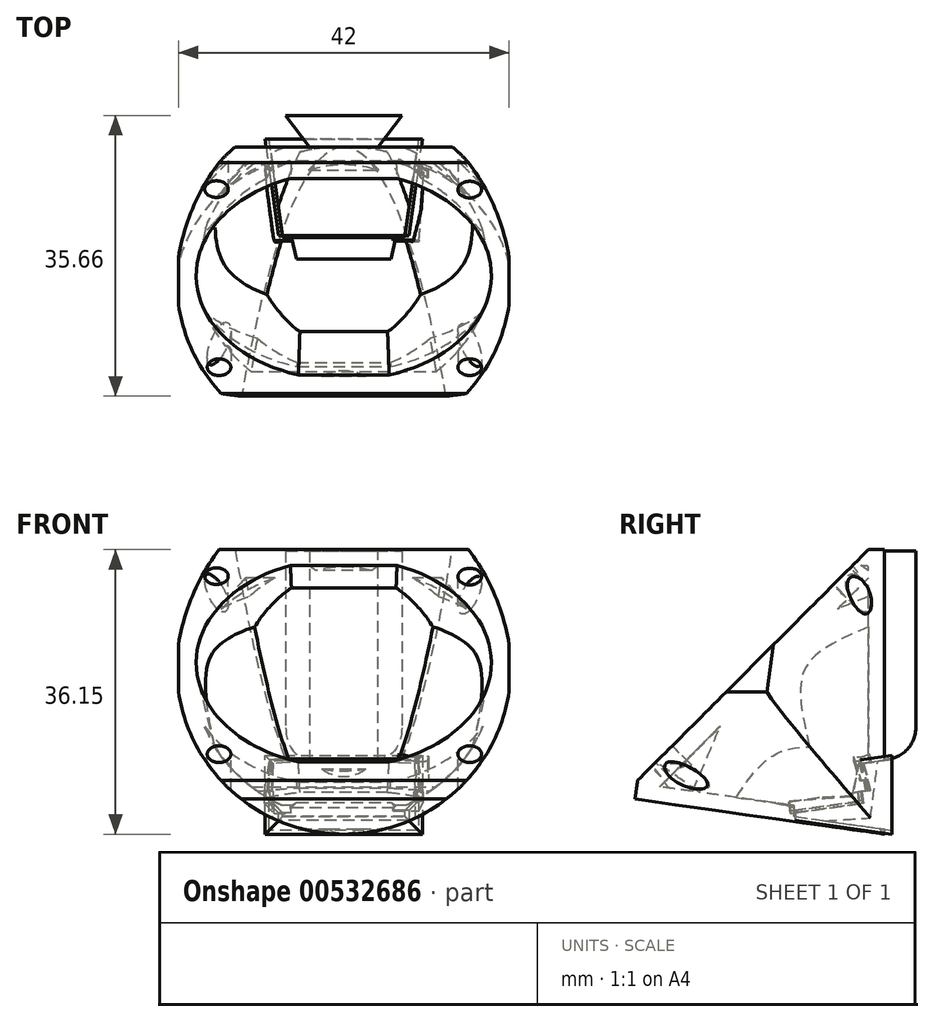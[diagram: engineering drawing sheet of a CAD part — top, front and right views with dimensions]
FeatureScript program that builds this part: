
annotation { "Feature Type Name" : "Feature", "Feature Type Description" : "" }
export const myFeature = defineFeature(function(context is Context, id is Id, definition is map)
    precondition{}
    {
        {
            var Q0;
            Q0=qCreatedBy(makeId("Right.planeOp"),FACE);
            var sketch = newSketch(context, id + "F0", { "sketchPlane" : qUnion([Q0])});
            skLineSegment(sketch, "E0", {"start": v(-2, 36.15) * mm, "end": v(-31.7, 6.45) * mm});
            skLineSegment(sketch, "E1", {"start": v(-31.7, 6.45) * mm, "end": v(-31.66, 4.45) * mm});
            skLineSegment(sketch, "E2", {"start": v(-31.66, 4.45) * mm, "end": v(0, 0) * mm});
            skLineSegment(sketch, "E3", {"start": v(0, 0) * mm, "end": v(0, 36.15) * mm});
            skLineSegment(sketch, "E4", {"start": v(0, 36.15) * mm, "end": v(-2, 36.15) * mm});
            skSolve(sketch);
        }
        {
            var Q0;
            Q0 = qSketchRegion(id + "F0", true);
            extrude(context, id + "F1", {"entities" : qUnion([Q0]), "endBound" : BoundingType.SYMMETRIC, "depth" : 42 * mm, "offsetDistance" : 25 * mm});
        }
        {
            var Q0;
            Q0=makeQuery(id+"F1.opExtrude","SWEPT_FACE",FACE,{"disambiguationData":[OSD([sQuery(id+"F0.wireOp",EDGE,"E2")])]});
            var sketch = newSketch(context, id + "F2", { "sketchPlane" : qUnion([Q0])});
            skLineSegment(sketch, "E5.bottom", {"start": v(-21, 31.98) * mm, "end": v(21, 31.98) * mm});
            skLineSegment(sketch, "E5.left", {"start": v(-21, 31.98) * mm, "end": v(-21, 17.27) * mm});
            skLineSegment(sketch, "E5.right", {"start": v(21, 31.98) * mm, "end": v(21, 17.27) * mm});
            skArc(sketch, "E6", {"start": v(-21, 17.27) * mm, "mid": v(0, 0) * mm, "end": v(21, 17.27) * mm});
            skSolve(sketch);
        }
        {
            var Q0;
            Q0=makeQuery(id+"F1.opExtrude","SWEPT_FACE",FACE,{"disambiguationData":[OSD([sQuery(id+"F0.wireOp",EDGE,"E3")])]});
            var sketch = newSketch(context, id + "F3", { "sketchPlane" : qUnion([Q0])});
            skLineSegment(sketch, "E7.bottom", {"start": v(-21, 36.15) * mm, "end": v(21, 36.15) * mm});
            skLineSegment(sketch, "E7.left", {"start": v(-21, 36.15) * mm, "end": v(-21, 18.07) * mm});
            skLineSegment(sketch, "E7.right", {"start": v(21, 36.15) * mm, "end": v(21, 18.07) * mm});
            skArc(sketch, "E8", {"start": v(-21, 18.07) * mm, "mid": v(0, 0) * mm, "end": v(21, 18.07) * mm});
            skSolve(sketch);
        }
        {
            var Q0;
            Q0=makeQuery(id+"F2.imprint","IMPRINT",FACE,{"disambiguationData":[TD([[makeQuery(id+"F2.imprint","IMPRINT",EDGE,{"derivedFrom":sQuery(id+"F2.wireOp",EDGE,"E5.bottom")}),1.0]])]});
            extrude(context, id + "F4", {"entities" : qUnion([Q0]), "operationType" : NewBodyOperationType.INTERSECT, "oppositeDirection" : true, "depth" : 46 * mm, "offsetDistance" : 25 * mm});
        }
        {
            var Q0;
            Q0=makeQuery(id+"F3.imprint","IMPRINT",FACE,{"disambiguationData":[TD([[makeQuery(id+"F3.imprint","IMPRINT",EDGE,{"derivedFrom":sQuery(id+"F3.wireOp",EDGE,"E7.bottom")}),-1.0]])]});
            extrude(context, id + "F5", {"entities" : qUnion([Q0]), "operationType" : NewBodyOperationType.INTERSECT, "oppositeDirection" : true, "depth" : 50 * mm, "offsetDistance" : 25 * mm});
        }
        {
            var Q0;
            Q0=makeQuery(id+"F1.opExtrude","SWEPT_FACE",FACE,{"disambiguationData":[OSD([sQuery(id+"F0.wireOp",EDGE,"E0")])]});
            shell(context, id + "F6", {"entities" : qUnion([Q0]), "thickness" : 2 * mm});
        }
        {
            var Q0;
            Q0=makeQuery(id+"F1.opExtrude","SWEPT_FACE",FACE,{"disambiguationData":[OSD([sQuery(id+"F0.wireOp",EDGE,"E0")])]});
            var sketch = newSketch(context, id + "F7", { "sketchPlane" : qUnion([Q0])});
            skLineSegment(sketch, "E9.bottom", {"start": v(-21, 24.54) * mm, "end": v(21, 24.54) * mm});
            skLineSegment(sketch, "E9.top", {"start": v(-21, -17.46) * mm, "end": v(21, -17.46) * mm});
            skLineSegment(sketch, "E9.left", {"start": v(-21, 24.54) * mm, "end": v(-21, -17.46) * mm});
            skLineSegment(sketch, "E9.right", {"start": v(21, 24.54) * mm, "end": v(21, -17.46) * mm});
            skCircle(sketch, "E10", {"center": v(0, 3.83) * mm, "radius": 18.75 * mm});
            skLineSegment(sketch, "E11", {"start": v(-14.68, 21.32) * mm, "end": v(14.98, -14.01) * mm, "construction": true});
            skLineSegment(sketch, "E12", {"start": v(14.68, 21.32) * mm, "end": v(-14.98, -14.01) * mm, "construction": true});
            skSolve(sketch);
        }
        {
            var Q0;
            {var subQ0=sQuery(id+"F0.wireOp",EDGE,"E0");Q0=makeQuery(id+"F7.imprint","IMPRINT",FACE,{"disambiguationData":[TD([[makeQuery(id+"F7.imprint","IMPRINT",EDGE,{"derivedFrom":makeQuery(id+"F6.opShell","OFFSET_EDGE",EDGE,{"disambiguationData":[OSD([subQ0]),TDD([makeQuery(id+"F1.opExtrude","CAP_EDGE",EDGE,{"disambiguationData":[OSD([subQ0])],"isStart":true})])]})}),1.0]])]});}
            var Q1;
            {var subQ2=sQuery(id+"F0.wireOp",EDGE,"E0");Q1=makeQuery(id+"F7.imprint","IMPRINT",FACE,{"disambiguationData":[TD([[makeQuery(id+"F7.imprint","IMPRINT",EDGE,{"derivedFrom":makeQuery(id+"F6.opShell","OFFSET_EDGE",EDGE,{"disambiguationData":[OSD([subQ2]),TDD([makeQuery(id+"F1.opExtrude","CAP_EDGE",EDGE,{"disambiguationData":[OSD([subQ2])],"isStart":true})])]})}),-1.0]])]});}
            var Q2;
            {var subQ1=sQuery(id+"F0.wireOp",EDGE,"E0");Q2=makeQuery(id+"F7.imprint","IMPRINT",FACE,{"disambiguationData":[TD([[makeQuery(id+"F7.imprint","IMPRINT",EDGE,{"derivedFrom":makeQuery(id+"F6.opShell","OFFSET_EDGE",EDGE,{"disambiguationData":[OSD([subQ1]),TDD([makeQuery(id+"F1.opExtrude","CAP_EDGE",EDGE,{"disambiguationData":[OSD([subQ1])],"isStart":false})])]})}),-1.0]])]});}
            extrude(context, id + "F8", {"entities" : qUnion([Q0, Q1, Q2]), "operationType" : NewBodyOperationType.ADD, "oppositeDirection" : true, "depth" : 2.55 * mm, "offsetDistance" : 25 * mm});
        }
        {
            var Q0;
            Q0=makeQuery(id+"F2.imprint","IMPRINT",FACE,{"disambiguationData":[TD([[makeQuery(id+"F2.imprint","IMPRINT",EDGE,{"derivedFrom":sQuery(id+"F2.wireOp",EDGE,"E5.bottom")}),1.0]])]});
            extrude(context, id + "F9", {"entities" : qUnion([Q0]), "operationType" : NewBodyOperationType.INTERSECT, "oppositeDirection" : true, "depth" : 50 * mm, "offsetDistance" : 25 * mm});
        }
        {
            var Q0;
            Q0=makeQuery(id+"F3.imprint","IMPRINT",FACE,{"disambiguationData":[TD([[makeQuery(id+"F3.imprint","IMPRINT",EDGE,{"derivedFrom":sQuery(id+"F3.wireOp",EDGE,"E7.bottom")}),-1.0]])]});
            extrude(context, id + "F10", {"entities" : qUnion([Q0]), "operationType" : NewBodyOperationType.INTERSECT, "oppositeDirection" : true, "depth" : 50 * mm, "offsetDistance" : 25 * mm});
        }
        {
            var Q0;
            Q0=makeQuery(id+"F3.imprint","IMPRINT",FACE,{"disambiguationData":[TD([[makeQuery(id+"F3.imprint","IMPRINT",EDGE,{"derivedFrom":sQuery(id+"F3.wireOp",EDGE,"E7.bottom")}),-1.0]])]});
            var sketch = newSketch(context, id + "F11", { "sketchPlane" : qUnion([Q0])});
            skLineSegment(sketch, "E13", {"start": v(0, 57.2) * mm, "end": v(0, -17.95) * mm, "construction": true});
            skLineSegment(sketch, "E14", {"start": v(-41.9, 22.75) * mm, "end": v(48.28, 22.75) * mm, "construction": true});
            skLineSegment(sketch, "E15.bottom", {"start": v(7.37, 36) * mm, "end": v(-7.38, 36) * mm});
            skLineSegment(sketch, "E15.top", {"start": v(7.38, 9.5) * mm, "end": v(-7.38, 9.5) * mm});
            skLineSegment(sketch, "E15.left", {"start": v(7.38, 36) * mm, "end": v(7.38, 9.5) * mm});
            skLineSegment(sketch, "E15.right", {"start": v(-7.38, 36) * mm, "end": v(-7.38, 9.5) * mm});
            skPoint(sketch, "E15.middle", {"position": v(0, 22.75) * mm});
            skSolve(sketch);
        }
        {
            var Q0;
            Q0 = qSketchRegion(id + "F11", true);
            extrude(context, id + "F12", {"entities" : qUnion([Q0]), "depth" : 4 * mm, "offsetDistance" : 25 * mm});
        }
        {
            var Q0;
            Q0=makeQuery(id+"F12.opExtrude","CAP_EDGE",EDGE,{"disambiguationData":[OSD([sQuery(id+"F11.wireOp",EDGE,"E15.right")])],"isStart":true});
            var Q1;
            Q1=makeQuery(id+"F12.opExtrude","CAP_EDGE",EDGE,{"disambiguationData":[OSD([sQuery(id+"F11.wireOp",EDGE,"E15.left")])],"isStart":true});
            chamfer(context, id + "F13", {"entities" : qUnion([Q0, Q1]), "chamferType" : ChamferType.TWO_OFFSETS, "width1" : 4 * mm, "oppositeDirection" : false, "width2" : 3 * mm, "tangentPropagation" : true});
        }
        {
            var Q0;
            {var subQ0=sQuery(id+"F0.wireOp",EDGE,"E0");Q0=makeQuery(id+"F8.boolean.opBoolean","MERGE",FACE,{"derivedFrom":[makeQuery(id+"F1.opExtrude","SWEPT_FACE",FACE,{"disambiguationData":[OSD([subQ0])]}),makeQuery(id+"F8.opExtrude","CAP_FACE",FACE,{"disambiguationData":[OSD([subQ0,sQuery(id+"F0.wireOp",EDGE,"E4"),sQuery(id+"F2.wireOp",EDGE,"E5.bottom"),sQuery(id+"F2.wireOp",EDGE,"E6"),sQuery(id+"F3.wireOp",EDGE,"E8"),sQuery(id+"F7.wireOp",EDGE,"E9.left"),sQuery(id+"F7.wireOp",EDGE,"E9.right"),sQuery(id+"F7.wireOp",EDGE,"E10")])],"isStart":true})]});}
            var sketch = newSketch(context, id + "F14", { "sketchPlane" : qUnion([Q0])});
            skArc(sketch, "E16.0", {"start": v(-6.88, 21.92) * mm, "mid": v(-19.34, 3.29) * mm, "end": v(-5.85, -14.61) * mm});
            skLineSegment(sketch, "E16.1", {"start": v(6.88, 21.92) * mm, "end": v(-6.88, 21.92) * mm});
            skArc(sketch, "E16.2", {"start": v(5.85, -14.61) * mm, "mid": v(19.34, 3.29) * mm, "end": v(6.88, 21.92) * mm});
            skLineSegment(sketch, "E16.3", {"start": v(5.85, -14.61) * mm, "end": v(-5.85, -14.61) * mm});
            skArc(sketch, "E17.0", {"start": v(-6.77, 21.32) * mm, "mid": v(-18.74, 3.3) * mm, "end": v(-5.76, -14.01) * mm});
            skLineSegment(sketch, "E18.0", {"start": v(6.77, 21.32) * mm, "end": v(-6.77, 21.32) * mm});
            skArc(sketch, "E19.0", {"start": v(5.76, -14.01) * mm, "mid": v(18.74, 3.3) * mm, "end": v(6.77, 21.32) * mm});
            skLineSegment(sketch, "E20.0", {"start": v(5.76, -14.01) * mm, "end": v(-5.76, -14.01) * mm});
            skSolve(sketch);
        }
        {
            var Q0;
            Q0=makeQuery(id+"F14.imprint","IMPRINT",FACE,{"disambiguationData":[TD([[makeQuery(id+"F14.imprint","IMPRINT",EDGE,{"derivedFrom":sQuery(id+"F14.wireOp",EDGE,"E16.0")}),1.0]])]});
            var Q1;
            Q1=makeQuery(id+"F6.opShell","OFFSET_FACE",FACE,{"disambiguationData":[OSD([sQuery(id+"F0.wireOp",EDGE,"E3")])]});
            var Q2;
            Q2=makeQuery(id+"F1.opExtrude","SWEPT_BODY",BODY,{"disambiguationData":[OSD([sQuery(id+"F0.wireOp",EDGE,"E0"),sQuery(id+"F0.wireOp",EDGE,"E1"),sQuery(id+"F0.wireOp",EDGE,"E2"),sQuery(id+"F0.wireOp",EDGE,"E3"),sQuery(id+"F0.wireOp",EDGE,"E4")])]});
            extrude(context, id + "F15", {"entities" : qUnion([Q0]), "operationType" : NewBodyOperationType.ADD, "endBound" : BoundingType.UP_TO_BODY, "oppositeDirection" : true, "depth" : 4.5 * mm, "endBoundEntityFace" : qUnion([Q1]), "endBoundEntityBody" : qUnion([Q2]), "offsetDistance" : 25 * mm, "hasDraft" : true, "draftAngle" : 10 * degree});
        }
        {
            var Q0;
            Q0=qCreatedBy(makeId("Front.planeOp"),FACE);
            cPlane(context, id + "F16", {"entities" : qUnion([Q0]), "cplaneType" : CPlaneType.OFFSET, "offset" : 1 * mm, "oppositeDirection" : true, "width" : 150 * mm, "height" : 150 * mm});
        }
        {
            var Q0;
            Q0=qCreatedBy(id+"F16.planeOp",FACE);
            var sketch = newSketch(context, id + "F17", { "sketchPlane" : qUnion([Q0])});
            skLineSegment(sketch, "E21.bottom", {"start": v(-10, 10) * mm, "end": v(10, 10) * mm});
            skLineSegment(sketch, "E21.top", {"start": v(-10, 0) * mm, "end": v(10, 0) * mm});
            skLineSegment(sketch, "E21.left", {"start": v(-10, 10) * mm, "end": v(-10, 0) * mm});
            skLineSegment(sketch, "E21.right", {"start": v(10, 10) * mm, "end": v(10, 0) * mm});
            skSolve(sketch);
        }
        {
            var Q0;
            Q0=makeQuery(id+"F17.imprint","IMPRINT",FACE,{"disambiguationData":[TD([[makeQuery(id+"F17.imprint","IMPRINT",EDGE,{"derivedFrom":sQuery(id+"F17.wireOp",EDGE,"E21.bottom")}),-1.0]])]});
            var Q1;
            Q1=makeQuery(id+"F1.opExtrude","SWEPT_BODY",BODY,{"disambiguationData":[OSD([sQuery(id+"F0.wireOp",EDGE,"E0"),sQuery(id+"F0.wireOp",EDGE,"E1"),sQuery(id+"F0.wireOp",EDGE,"E2"),sQuery(id+"F0.wireOp",EDGE,"E3"),sQuery(id+"F0.wireOp",EDGE,"E4")])]});
            extrude(context, id + "F18", {"entities" : qUnion([Q0]), "depth" : 12.27 * mm, "endBoundEntityBody" : qUnion([Q1]), "offsetDistance" : 25 * mm, "hasDraft" : true, "draftAngle" : 8 * degree, "draftPullDirection" : true});
        }
        {
            var Q0;
            Q0=makeQuery(id+"F17.imprint","IMPRINT",FACE,{"disambiguationData":[TD([[makeQuery(id+"F17.imprint","IMPRINT",EDGE,{"derivedFrom":sQuery(id+"F17.wireOp",EDGE,"E21.bottom")}),-1.0]])]});
            var sketch = newSketch(context, id + "F19", { "sketchPlane" : qUnion([Q0])});
            skLineSegment(sketch, "E22.bottom", {"start": v(9.5, 9.5) * mm, "end": v(-9.5, 9.5) * mm});
            skLineSegment(sketch, "E22.top", {"start": v(9.5, 0.5) * mm, "end": v(-9.5, 0.5) * mm});
            skLineSegment(sketch, "E22.left", {"start": v(9.5, 9.5) * mm, "end": v(9.5, 0.5) * mm});
            skLineSegment(sketch, "E22.right", {"start": v(-9.5, 9.5) * mm, "end": v(-9.5, 0.5) * mm});
            skSolve(sketch);
        }
        {
            var Q0;
            Q0 = qSketchRegion(id + "F19", true);
            extrude(context, id + "F20", {"entities" : qUnion([Q0]), "operationType" : NewBodyOperationType.REMOVE, "endBound" : BoundingType.SYMMETRIC, "depth" : 25 * mm, "offsetDistance" : 25 * mm, "hasDraft" : true, "draftAngle" : 8 * degree, "draftPullDirection" : true});
        }
        {
            var Q0;
            Q0=makeQuery(id+"F18.opExtrude","SWEPT_FACE",FACE,{"disambiguationData":[OSD([sQuery(id+"F17.wireOp",EDGE,"E21.bottom")])]});
            var sketch = newSketch(context, id + "F21", { "sketchPlane" : qUnion([Q0])});
            skLineSegment(sketch, "E23", {"start": v(8.28, -10) * mm, "end": v(-8.28, -10) * mm});
            skLineSegment(sketch, "E24", {"start": v(-8.28, -10) * mm, "end": v(-9.43, -1.73) * mm});
            skLineSegment(sketch, "E25", {"start": v(-9.43, -1.73) * mm, "end": v(-7.08, -0.58) * mm});
            skLineSegment(sketch, "E26", {"start": v(-7.08, -0.58) * mm, "end": v(7.03, -0.58) * mm});
            skLineSegment(sketch, "E27", {"start": v(7.03, -0.58) * mm, "end": v(9.4, -1.9) * mm});
            skLineSegment(sketch, "E28", {"start": v(9.4, -1.9) * mm, "end": v(8.28, -10) * mm});
            skSolve(sketch);
        }
        {
            var Q0;
            Q0 = qSketchRegion(id + "F21", true);
            extrude(context, id + "F22", {"entities" : qUnion([Q0]), "operationType" : NewBodyOperationType.REMOVE, "oppositeDirection" : true, "depth" : 4 * mm, "offsetDistance" : 25 * mm, "hasDraft" : true, "draftAngle" : 8 * degree});
        }
        {
            var Q0;
            Q0 = qSketchRegion(id + "F19", true);
            extrude(context, id + "F23", {"entities" : qUnion([Q0]), "operationType" : NewBodyOperationType.REMOVE, "depth" : 16 * mm, "offsetDistance" : 25 * mm, "hasDraft" : true, "draftAngle" : 13 * degree, "draftPullDirection" : true});
        }
        {
            var Q0;
            {var subQ0=sQuery(id+"F17.wireOp",EDGE,"E21.left");var subQ1=sQuery(id+"F21.wireOp",EDGE,"E25");Q0=makeQuery(id+"F22.boolean.opBoolean","COPY",FACE,{"disambiguationData":[TD([makeQuery(id+"F18.opExtrude","SWEPT_FACE",FACE,{"disambiguationData":[OSD([subQ0])]})])],"derivedFrom":makeQuery(id+"F22.opExtrude","CAP_FACE",FACE,{"disambiguationData":[OSD([sQuery(id+"F21.wireOp",EDGE,"E23"),sQuery(id+"F21.wireOp",EDGE,"E24"),subQ1,sQuery(id+"F21.wireOp",EDGE,"E26"),sQuery(id+"F21.wireOp",EDGE,"E27"),sQuery(id+"F21.wireOp",EDGE,"E28")])],"isStart":false})});}
            var sketch = newSketch(context, id + "F24", { "sketchPlane" : qUnion([Q0])});
            skLineSegment(sketch, "E29", {"start": v(-8.88, -11.43) * mm, "end": v(-6.68, -11.34) * mm});
            skLineSegment(sketch, "E30", {"start": v(-6.68, -11.34) * mm, "end": v(-7.87, -1.93) * mm});
            skLineSegment(sketch, "E31", {"start": v(-7.87, -1.93) * mm, "end": v(-10.08, -2.21) * mm});
            skLineSegment(sketch, "E32", {"start": v(-10.08, -2.21) * mm, "end": v(-8.88, -11.43) * mm});
            skSolve(sketch);
        }
        {
            var Q0;
            Q0 = qSketchRegion(id + "F24", true);
            extrude(context, id + "F25", {"entities" : qUnion([Q0]), "operationType" : NewBodyOperationType.REMOVE, "oppositeDirection" : true, "depth" : 1.5 * mm, "offsetDistance" : 25 * mm});
        }
        {
            var Q0;
            {var subQ0=sQuery(id+"F17.wireOp",EDGE,"E21.right");var subQ1=sQuery(id+"F21.wireOp",EDGE,"E27");Q0=makeQuery(id+"F22.boolean.opBoolean","COPY",FACE,{"disambiguationData":[TD([makeQuery(id+"F18.opExtrude","SWEPT_FACE",FACE,{"disambiguationData":[OSD([subQ0])]})])],"derivedFrom":makeQuery(id+"F22.opExtrude","CAP_FACE",FACE,{"disambiguationData":[OSD([sQuery(id+"F21.wireOp",EDGE,"E23"),sQuery(id+"F21.wireOp",EDGE,"E24"),sQuery(id+"F21.wireOp",EDGE,"E25"),sQuery(id+"F21.wireOp",EDGE,"E26"),subQ1,sQuery(id+"F21.wireOp",EDGE,"E28")])],"isStart":false})});}
            var sketch = newSketch(context, id + "F26", { "sketchPlane" : qUnion([Q0])});
            skLineSegment(sketch, "E33", {"start": v(6.24, -11.32) * mm, "end": v(9.58, -11.32) * mm});
            skLineSegment(sketch, "E34", {"start": v(9.58, -11.32) * mm, "end": v(10.15, -2.6) * mm});
            skLineSegment(sketch, "E35", {"start": v(10.15, -2.6) * mm, "end": v(7.91, -2.45) * mm});
            skLineSegment(sketch, "E36", {"start": v(7.91, -2.45) * mm, "end": v(6.24, -11.32) * mm});
            skSolve(sketch);
        }
        {
            var Q0;
            Q0 = qSketchRegion(id + "F26", true);
            extrude(context, id + "F27", {"entities" : qUnion([Q0]), "operationType" : NewBodyOperationType.REMOVE, "oppositeDirection" : true, "depth" : 1.2 * mm, "offsetDistance" : 25 * mm});
        }
        {
            var Q0;
            Q0=makeQuery(id+"F22.boolean.opBoolean","COPY",FACE,{"derivedFrom":makeQuery(id+"F22.opExtrude","SWEPT_FACE",FACE,{"disambiguationData":[OSD([sQuery(id+"F21.wireOp",EDGE,"E27")])]})});
            var sketch = newSketch(context, id + "F28", { "sketchPlane" : qUnion([Q0])});
            skLineSegment(sketch, "E37", {"start": v(5.52, 10.21) * mm, "end": v(9.81, 10.89) * mm});
            skLineSegment(sketch, "E38", {"start": v(9.81, 10.89) * mm, "end": v(9.81, 7.44) * mm});
            skLineSegment(sketch, "E39", {"start": v(9.81, 7.44) * mm, "end": v(5.9, 6.97) * mm});
            skLineSegment(sketch, "E40", {"start": v(5.9, 6.97) * mm, "end": v(5.52, 10.21) * mm});
            skSolve(sketch);
        }
        {
            var Q0;
            Q0 = qSketchRegion(id + "F28", true);
            extrude(context, id + "F29", {"entities" : qUnion([Q0]), "operationType" : NewBodyOperationType.REMOVE, "oppositeDirection" : true, "depth" : .2 * mm, "offsetDistance" : 25 * mm});
        }
        {
            var Q0;
            Q0=makeQuery(id+"F12.opExtrude","CAP_EDGE",EDGE,{"disambiguationData":[OSD([sQuery(id+"F11.wireOp",EDGE,"E15.top")])],"isStart":false});
            fillet(context, id + "F30", {"entities" : qUnion([Q0]), "radius" : 4 * mm, "tangentPropagation" : true, "allowEdgeOverflow" : false});
        }
        {
            var Q0;
            {var subQ0=sQuery(id+"F0.wireOp",EDGE,"E0");Q0=makeQuery(id+"F8.boolean.opBoolean","MERGE",FACE,{"derivedFrom":[makeQuery(id+"F1.opExtrude","SWEPT_FACE",FACE,{"disambiguationData":[OSD([subQ0])]}),makeQuery(id+"F8.opExtrude","CAP_FACE",FACE,{"disambiguationData":[OSD([subQ0,sQuery(id+"F0.wireOp",EDGE,"E4"),sQuery(id+"F2.wireOp",EDGE,"E5.bottom"),sQuery(id+"F2.wireOp",EDGE,"E6"),sQuery(id+"F3.wireOp",EDGE,"E8"),sQuery(id+"F7.wireOp",EDGE,"E9.left"),sQuery(id+"F7.wireOp",EDGE,"E9.right"),sQuery(id+"F7.wireOp",EDGE,"E10")])],"isStart":true})]});}
            var sketch = newSketch(context, id + "F31", { "sketchPlane" : qUnion([Q0])});
            skLineSegment(sketch, "E41", {"start": v(-23.74, 24.15) * mm, "end": v(26.49, 24.15) * mm, "construction": true});
            skLineSegment(sketch, "E42", {"start": v(-31.74, -17.36) * mm, "end": v(33.17, -17.36) * mm, "construction": true});
            skLineSegment(sketch, "E43", {"start": v(-38.9, 3.4) * mm, "end": v(43.9, 3.4) * mm, "construction": true});
            skLineSegment(sketch, "E44", {"start": v(24.8, 3.4) * mm, "end": v(24.8, -17.36) * mm, "construction": true});
            skLineSegment(sketch, "E45", {"start": v(24.8, 3.4) * mm, "end": v(24.8, 24.15) * mm, "construction": true});
            skLineSegment(sketch, "E46", {"start": v(21.26, 19.3) * mm, "end": v(-29.68, 19.3) * mm, "construction": true});
            skLineSegment(sketch, "E47", {"start": v(-28.4, -12.6) * mm, "end": v(22.67, -12.6) * mm, "construction": true});
            skLineSegment(sketch, "E48", {"start": v(21, 33.83) * mm, "end": v(21, -33.33) * mm, "construction": true});
            skLineSegment(sketch, "E49", {"start": v(-21, 37.04) * mm, "end": v(-21, -34.34) * mm, "construction": true});
            skLineSegment(sketch, "E50", {"start": v(0, 44.9) * mm, "end": v(0, -43) * mm, "construction": true});
            skLineSegment(sketch, "E51", {"start": v(0, -31.3) * mm, "end": v(-21, -31.3) * mm, "construction": true});
            skLineSegment(sketch, "E52", {"start": v(0, -31.3) * mm, "end": v(21, -31.3) * mm, "construction": true});
            skLineSegment(sketch, "E53", {"start": v(-16, 36.02) * mm, "end": v(-16, -26.58) * mm, "construction": true});
            skLineSegment(sketch, "E54", {"start": v(16, -26.58) * mm, "end": v(16, 37.2) * mm, "construction": true});
            skCircle(sketch, "E55", {"center": v(-16.17, 19.38) * mm, "radius": 1.5 * mm});
            skCircle(sketch, "E56", {"center": v(16, 19.3) * mm, "radius": 1.5 * mm});
            skCircle(sketch, "E57", {"center": v(16, -12.6) * mm, "radius": 1.5 * mm});
            skCircle(sketch, "E58", {"center": v(-15.84, -12.6) * mm, "radius": 1.5 * mm});
            skSolve(sketch);
        }
        {
            var Q0;
            Q0=makeQuery(id+"F31.imprint","IMPRINT",FACE,{"disambiguationData":[TD([[makeQuery(id+"F31.imprint","IMPRINT",EDGE,{"derivedFrom":sQuery(id+"F31.wireOp",EDGE,"E56")}),1.0]])]});
            var Q1;
            Q1=makeQuery(id+"F31.imprint","IMPRINT",FACE,{"disambiguationData":[TD([[makeQuery(id+"F31.imprint","IMPRINT",EDGE,{"derivedFrom":sQuery(id+"F31.wireOp",EDGE,"E57")}),1.0]])]});
            var Q2;
            Q2=makeQuery(id+"F31.imprint","IMPRINT",FACE,{"disambiguationData":[TD([[makeQuery(id+"F31.imprint","IMPRINT",EDGE,{"derivedFrom":sQuery(id+"F31.wireOp",EDGE,"E58")}),1.0]])]});
            var Q3;
            Q3=makeQuery(id+"F31.imprint","IMPRINT",FACE,{"disambiguationData":[TD([[makeQuery(id+"F31.imprint","IMPRINT",EDGE,{"derivedFrom":sQuery(id+"F31.wireOp",EDGE,"E55")}),1.0]])]});
            extrude(context, id + "F32", {"entities" : qUnion([Q0, Q1, Q2, Q3]), "operationType" : NewBodyOperationType.REMOVE, "endBound" : BoundingType.SYMMETRIC, "oppositeDirection" : true, "depth" : 20 * mm, "offsetDistance" : 25 * mm});
        }
    });
